# Revit family: Stratobrace
name_source: partatom
category: Generic Models
units: mm (PartAtom-declared; Revit-internal decimal feet)

## family parameters
Always vertical = Yes
Can host rebar = No
Cut with Voids When Loaded = No
Part Type = Normal
Room Calculation Point = No
Round Connector Dimension = Use Diameter
Shared = No
Work Plane-Based = Yes

## types (1)
- Stratobrace
    Brace Arm Material = Steel
    Compression Post Material = Steel
    Cross Tee Material = Steel
    Default Elevation = 2200 mm
    Description = Designed to lock into a two way suspended grid system to increase its ability to withstand lateral loads.
    IFCExportAs = IfcElementAssembly
    IFCExportType = BRACED_FRAME
    IFCName = Stratobrace
    Main Tee Material = Steel
    Manufacturer = Cold Rolled Systems
    Masterspec CBI = 3421
    Material = Grade 250 steel 2mm thick with yield strength of 250MPa.
    Model = StratoBrace (Rigid Ceiling Brace).
    Stratobrace Bracket Material = Steel
    URL = https://www.tris.co.nz

## geometry (parser evidence)
native form markers: Sweep x27
no freeform markers — native parametric forms only
